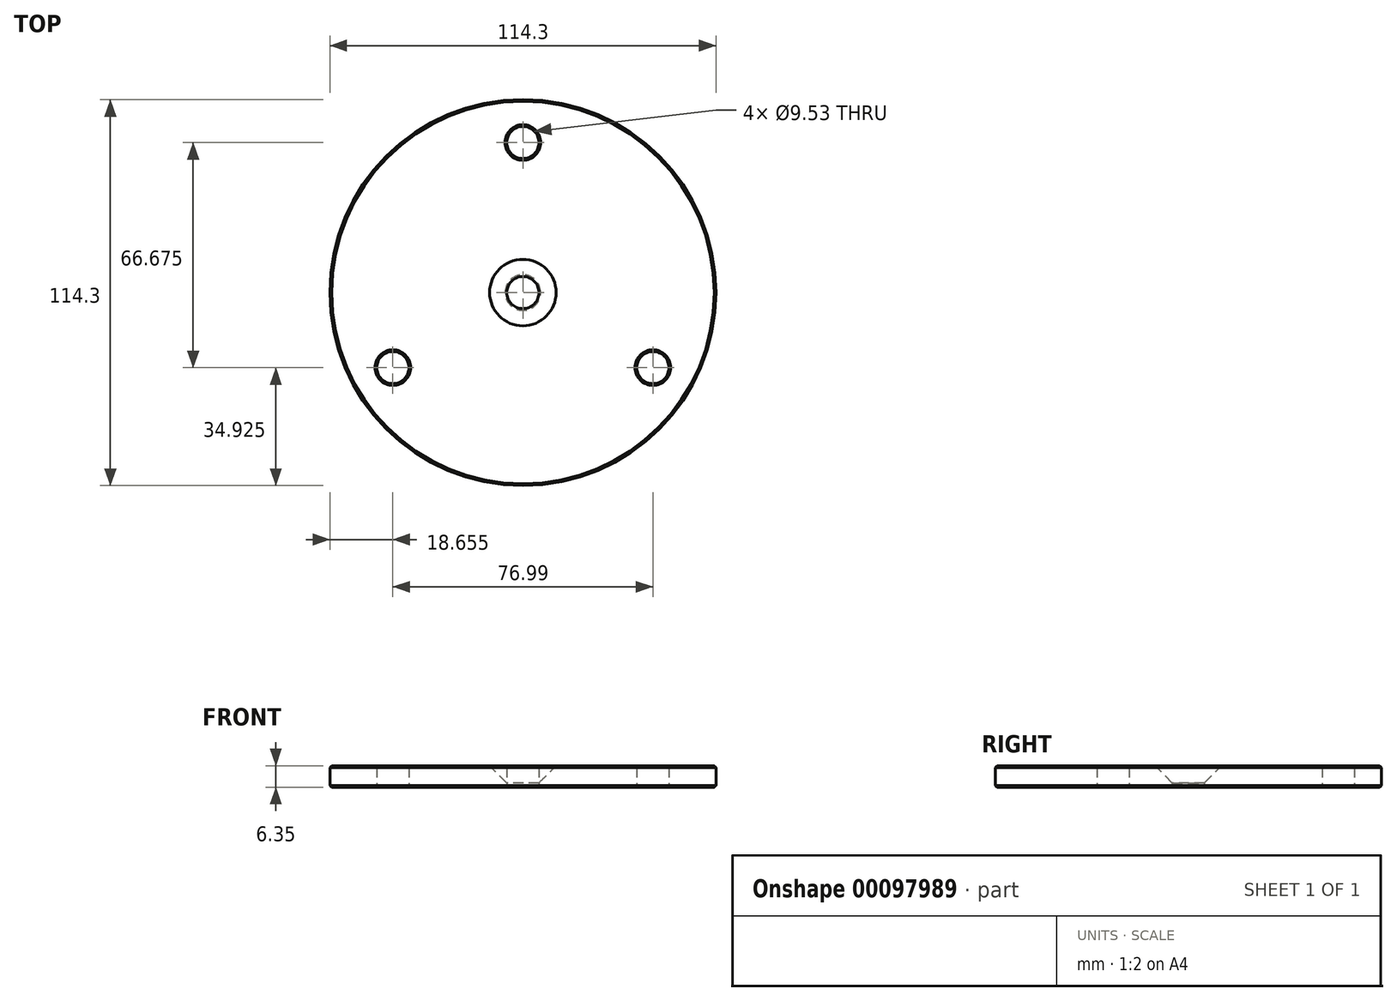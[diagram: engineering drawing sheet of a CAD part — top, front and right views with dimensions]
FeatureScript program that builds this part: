
annotation { "Feature Type Name" : "Feature", "Feature Type Description" : "" }
export const myFeature = defineFeature(function(context is Context, id is Id, definition is map)
    precondition{}
    {
        {
            var Q0;
            Q0=qCreatedBy(makeId("Top.planeOp"),FACE);
            var sketch = newSketch(context, id + "F0", { "sketchPlane" : qUnion([Q0])});
            skPoint(sketch, "E0.middle", {"position": v(0, 0) * mm});
            skLineSegment(sketch, "E1", {"start": v(0, 0) * mm, "end": v(0, 65.3) * mm, "construction": true});
            skLineSegment(sketch, "E2", {"start": v(0, 0) * mm, "end": v(-61.81, -35.69) * mm, "construction": true});
            skLineSegment(sketch, "E3", {"start": v(0, 0) * mm, "end": v(66.71, -38.52) * mm, "construction": true});
            skPoint(sketch, "E4.centerSnap0", {"position": v(0, 32.65) * mm});
            skPoint(sketch, "E5.visualSharp", {"position": v(24.59, -25.88) * mm});
            skPoint(sketch, "E6.visualSharp", {"position": v(-26.21, -25.88) * mm});
            skCircle(sketch, "E7", {"center": v(0, 0) * mm, "radius": 57.15 * mm});
            skCircle(sketch, "E8", {"center": v(0, 0) * mm, "radius": 4.76 * mm});
            skCircle(sketch, "E9", {"center": v(0, 44.45) * mm, "radius": 4.76 * mm});
            skCircle(sketch, "E10", {"center": v(-38.5, -22.22) * mm, "radius": 4.76 * mm});
            skCircle(sketch, "E11", {"center": v(38.5, -22.22) * mm, "radius": 4.76 * mm});
            skCircle(sketch, "E12", {"center": v(0, 0) * mm, "radius": 44.45 * mm, "construction": true});
            skSolve(sketch);
        }
        {
            var Q0;
            Q0=makeQuery(id+"F0.imprint","IMPRINT",FACE,{"disambiguationData":[TD([[makeQuery(id+"F0.imprint","IMPRINT",EDGE,{"derivedFrom":sQuery(id+"F0.wireOp",EDGE,"E7")}),1.0]])]});
            extrude(context, id + "F1", {"entities" : qUnion([Q0]), "depth" : 6.35 * mm});
        }
        {
            var Q0;
            Q0=makeQuery(id+"F1.opExtrude","CAP_EDGE",EDGE,{"disambiguationData":[OSD([sQuery(id+"F0.wireOp",EDGE,"E7")])],"isStart":false});
            var Q1;
            Q1=makeQuery(id+"F1.opExtrude","CAP_EDGE",EDGE,{"disambiguationData":[OSD([sQuery(id+"F0.wireOp",EDGE,"E9")])],"isStart":false});
            var Q2;
            Q2=makeQuery(id+"F1.opExtrude","CAP_EDGE",EDGE,{"disambiguationData":[OSD([sQuery(id+"F0.wireOp",EDGE,"E10")])],"isStart":false});
            var Q3;
            Q3=makeQuery(id+"F1.opExtrude","CAP_EDGE",EDGE,{"disambiguationData":[OSD([sQuery(id+"F0.wireOp",EDGE,"E11")])],"isStart":false});
            var Q4;
            Q4=makeQuery(id+"F1.opExtrude","CAP_EDGE",EDGE,{"disambiguationData":[OSD([sQuery(id+"F0.wireOp",EDGE,"E7")])],"isStart":true});
            var Q5;
            Q5=makeQuery(id+"F1.opExtrude","CAP_EDGE",EDGE,{"disambiguationData":[OSD([sQuery(id+"F0.wireOp",EDGE,"E9")])],"isStart":true});
            var Q6;
            Q6=makeQuery(id+"F1.opExtrude","CAP_EDGE",EDGE,{"disambiguationData":[OSD([sQuery(id+"F0.wireOp",EDGE,"E11")])],"isStart":true});
            var Q7;
            Q7=makeQuery(id+"F1.opExtrude","CAP_EDGE",EDGE,{"disambiguationData":[OSD([sQuery(id+"F0.wireOp",EDGE,"E10")])],"isStart":true});
            var Q8;
            Q8=makeQuery(id+"F1.opExtrude","CAP_EDGE",EDGE,{"disambiguationData":[OSD([sQuery(id+"F0.wireOp",EDGE,"E8")])],"isStart":true});
            chamfer(context, id + "F2", {"entities" : qUnion([Q0, Q1, Q2, Q3, Q4, Q5, Q6, Q7, Q8]), "width" : 0.5 * mm, "tangentPropagation" : true});
        }
        {
            var Q0;
            Q0=makeQuery(id+"F1.opExtrude","CAP_EDGE",EDGE,{"disambiguationData":[OSD([sQuery(id+"F0.wireOp",EDGE,"E8")])],"isStart":false});
            chamfer(context, id + "F3", {"entities" : qUnion([Q0]), "width" : 5.08 * mm, "tangentPropagation" : true});
        }
    });
